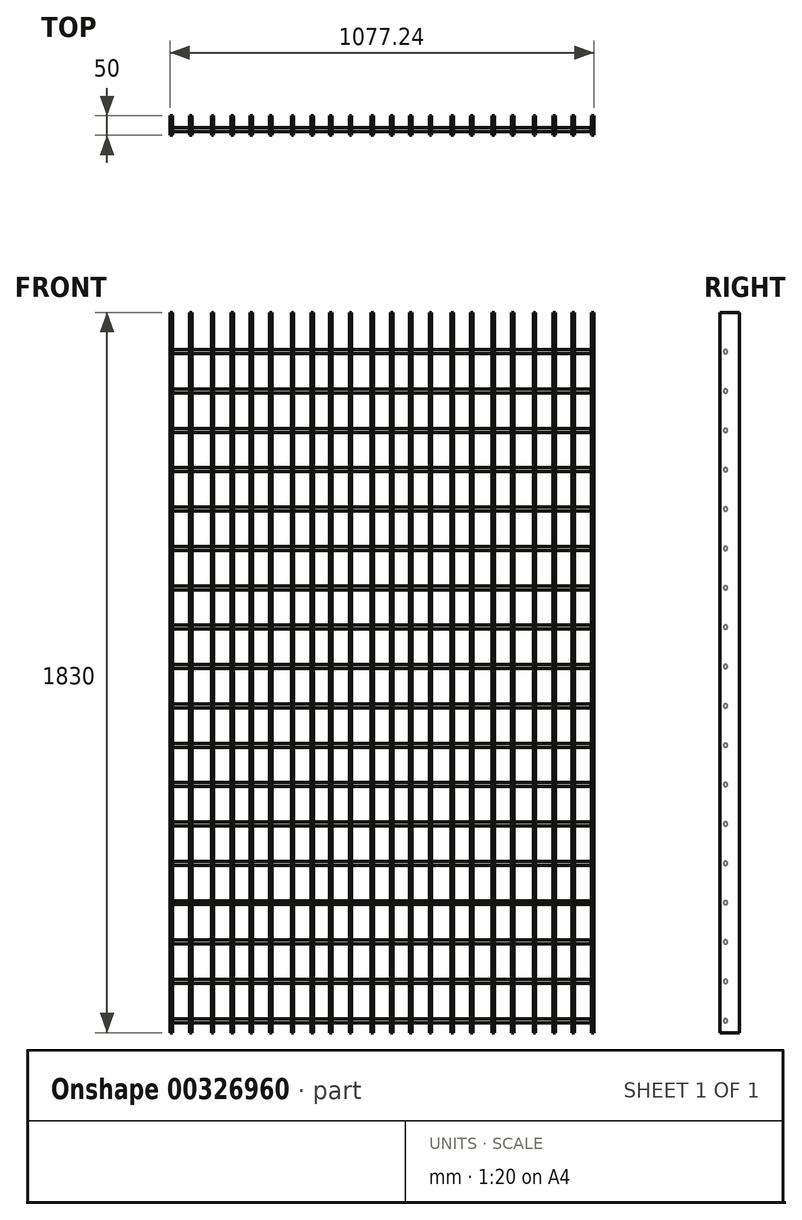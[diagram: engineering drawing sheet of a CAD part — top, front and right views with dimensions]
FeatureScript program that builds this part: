
annotation { "Feature Type Name" : "Feature", "Feature Type Description" : "" }
export const myFeature = defineFeature(function(context is Context, id is Id, definition is map)
    precondition{}
    {
        {
            var Q0;
            Q0=qCreatedBy(makeId("Front.planeOp"),FACE);
            var sketch = newSketch(context, id + "F0", { "sketchPlane" : qUnion([Q0])});
            skLineSegment(sketch, "E0.left", {"start": v(-535, -915) * mm, "end": v(-535, 915) * mm});
            skLineSegment(sketch, "E0.right", {"start": v(535, -915) * mm, "end": v(535, 915) * mm});
            skPoint(sketch, "E0.middle", {"position": v(0, 0) * mm});
            skLineSegment(sketch, "E1", {"start": v(-535, 915) * mm, "end": v(-529, 915) * mm});
            skLineSegment(sketch, "E2", {"start": v(-529, 915) * mm, "end": v(-529, -915) * mm});
            skLineSegment(sketch, "E3", {"start": v(-529, -915) * mm, "end": v(-535, -915) * mm});
            skLineSegment(sketch, "E4", {"start": v(-485, -915) * mm, "end": v(-485, 915) * mm});
            skLineSegment(sketch, "E5", {"start": v(-485, 915) * mm, "end": v(-479, 915) * mm});
            skLineSegment(sketch, "E6", {"start": v(-479, 915) * mm, "end": v(-479, -915) * mm});
            skLineSegment(sketch, "E7", {"start": v(-479, -915) * mm, "end": v(-485, -915) * mm});
            skLineSegment(sketch, "E8.left", {"start": v(-429.8, -915) * mm, "end": v(-429.8, 915) * mm});
            skLineSegment(sketch, "E9", {"start": v(-429.8, 915) * mm, "end": v(-423.8, 915) * mm});
            skLineSegment(sketch, "E10", {"start": v(-423.8, 915) * mm, "end": v(-423.8, -915) * mm});
            skLineSegment(sketch, "E11", {"start": v(-423.8, -915) * mm, "end": v(-429.8, -915) * mm});
            skLineSegment(sketch, "E12", {"start": v(-379.8, -915) * mm, "end": v(-379.8, 915) * mm});
            skLineSegment(sketch, "E13", {"start": v(-379.8, 915) * mm, "end": v(-373.8, 915) * mm});
            skLineSegment(sketch, "E14", {"start": v(-373.8, 915) * mm, "end": v(-373.8, -915) * mm});
            skLineSegment(sketch, "E15", {"start": v(-373.8, -915) * mm, "end": v(-379.8, -915) * mm});
            skLineSegment(sketch, "E16.left", {"start": v(-331.72, -915) * mm, "end": v(-331.72, 915) * mm});
            skLineSegment(sketch, "E17", {"start": v(-331.72, 915) * mm, "end": v(-325.72, 915) * mm});
            skLineSegment(sketch, "E18", {"start": v(-325.72, 915) * mm, "end": v(-325.72, -915) * mm});
            skLineSegment(sketch, "E19", {"start": v(-325.72, -915) * mm, "end": v(-331.72, -915) * mm});
            skLineSegment(sketch, "E20", {"start": v(-281.72, -915) * mm, "end": v(-281.72, 915) * mm});
            skLineSegment(sketch, "E21", {"start": v(-281.72, 915) * mm, "end": v(-275.72, 915) * mm});
            skLineSegment(sketch, "E22", {"start": v(-275.72, 915) * mm, "end": v(-275.72, -915) * mm});
            skLineSegment(sketch, "E23", {"start": v(-275.72, -915) * mm, "end": v(-281.72, -915) * mm});
            skLineSegment(sketch, "E24.left", {"start": v(-226.52, -915) * mm, "end": v(-226.52, 915) * mm});
            skLineSegment(sketch, "E25", {"start": v(-226.52, 915) * mm, "end": v(-220.52, 915) * mm});
            skLineSegment(sketch, "E26", {"start": v(-220.52, 915) * mm, "end": v(-220.52, -915) * mm});
            skLineSegment(sketch, "E27", {"start": v(-220.52, -915) * mm, "end": v(-226.52, -915) * mm});
            skLineSegment(sketch, "E28", {"start": v(-176.52, -915) * mm, "end": v(-176.52, 915) * mm});
            skLineSegment(sketch, "E29", {"start": v(-176.52, 915) * mm, "end": v(-170.52, 915) * mm});
            skLineSegment(sketch, "E30", {"start": v(-170.52, 915) * mm, "end": v(-170.52, -915) * mm});
            skLineSegment(sketch, "E31", {"start": v(-170.52, -915) * mm, "end": v(-176.52, -915) * mm});
            skLineSegment(sketch, "E32.left", {"start": v(-129.52, -915) * mm, "end": v(-129.52, 915) * mm});
            skLineSegment(sketch, "E33", {"start": v(-129.52, 915) * mm, "end": v(-123.52, 915) * mm});
            skLineSegment(sketch, "E34", {"start": v(-123.52, 915) * mm, "end": v(-123.52, -915) * mm});
            skLineSegment(sketch, "E35", {"start": v(-123.52, -915) * mm, "end": v(-129.52, -915) * mm});
            skLineSegment(sketch, "E36", {"start": v(-79.52, -915) * mm, "end": v(-79.52, 915) * mm});
            skLineSegment(sketch, "E37", {"start": v(-79.52, 915) * mm, "end": v(-73.52, 915) * mm});
            skLineSegment(sketch, "E38", {"start": v(-73.52, 915) * mm, "end": v(-73.52, -915) * mm});
            skLineSegment(sketch, "E39", {"start": v(-73.52, -915) * mm, "end": v(-79.52, -915) * mm});
            skLineSegment(sketch, "E40.left", {"start": v(-24.33, -915) * mm, "end": v(-24.33, 915) * mm});
            skLineSegment(sketch, "E41", {"start": v(-24.33, 915) * mm, "end": v(-18.33, 915) * mm});
            skLineSegment(sketch, "E42", {"start": v(-18.33, 915) * mm, "end": v(-18.33, -915) * mm});
            skLineSegment(sketch, "E43", {"start": v(-18.33, -915) * mm, "end": v(-24.33, -915) * mm});
            skLineSegment(sketch, "E44", {"start": v(25.67, -915) * mm, "end": v(25.67, 915) * mm});
            skLineSegment(sketch, "E45", {"start": v(25.67, 915) * mm, "end": v(31.67, 915) * mm});
            skLineSegment(sketch, "E46", {"start": v(31.67, 915) * mm, "end": v(31.67, -915) * mm});
            skLineSegment(sketch, "E47", {"start": v(31.67, -915) * mm, "end": v(25.67, -915) * mm});
            skLineSegment(sketch, "E48.left", {"start": v(73.76, -915) * mm, "end": v(73.76, 915) * mm});
            skLineSegment(sketch, "E49", {"start": v(73.76, 915) * mm, "end": v(79.76, 915) * mm});
            skLineSegment(sketch, "E50", {"start": v(79.76, 915) * mm, "end": v(79.76, -915) * mm});
            skLineSegment(sketch, "E51", {"start": v(79.76, -915) * mm, "end": v(73.76, -915) * mm});
            skLineSegment(sketch, "E52", {"start": v(123.76, -915) * mm, "end": v(123.76, 915) * mm});
            skLineSegment(sketch, "E53", {"start": v(123.76, 915) * mm, "end": v(129.76, 915) * mm});
            skLineSegment(sketch, "E54", {"start": v(129.76, 915) * mm, "end": v(129.76, -915) * mm});
            skLineSegment(sketch, "E55", {"start": v(129.76, -915) * mm, "end": v(123.76, -915) * mm});
            skLineSegment(sketch, "E56.left", {"start": v(178.95, -915) * mm, "end": v(178.95, 915) * mm});
            skLineSegment(sketch, "E57", {"start": v(178.95, 915) * mm, "end": v(184.95, 915) * mm});
            skLineSegment(sketch, "E58", {"start": v(184.95, 915) * mm, "end": v(184.95, -915) * mm});
            skLineSegment(sketch, "E59", {"start": v(184.95, -915) * mm, "end": v(178.95, -915) * mm});
            skLineSegment(sketch, "E60", {"start": v(228.95, -915) * mm, "end": v(228.95, 915) * mm});
            skLineSegment(sketch, "E61", {"start": v(228.95, 915) * mm, "end": v(234.95, 915) * mm});
            skLineSegment(sketch, "E62", {"start": v(234.95, 915) * mm, "end": v(234.95, -915) * mm});
            skLineSegment(sketch, "E63", {"start": v(234.95, -915) * mm, "end": v(228.95, -915) * mm});
            skLineSegment(sketch, "E64.left", {"start": v(282.95, -915) * mm, "end": v(282.95, 915) * mm});
            skLineSegment(sketch, "E65", {"start": v(282.95, 915) * mm, "end": v(288.95, 915) * mm});
            skLineSegment(sketch, "E66", {"start": v(288.95, 915) * mm, "end": v(288.95, -915) * mm});
            skLineSegment(sketch, "E67", {"start": v(288.95, -915) * mm, "end": v(282.95, -915) * mm});
            skLineSegment(sketch, "E68", {"start": v(332.95, -915) * mm, "end": v(332.95, 915) * mm});
            skLineSegment(sketch, "E69", {"start": v(332.95, 915) * mm, "end": v(338.95, 915) * mm});
            skLineSegment(sketch, "E70", {"start": v(338.95, 915) * mm, "end": v(338.95, -915) * mm});
            skLineSegment(sketch, "E71", {"start": v(338.95, -915) * mm, "end": v(332.95, -915) * mm});
            skLineSegment(sketch, "E72.left", {"start": v(388.15, -915) * mm, "end": v(388.15, 915) * mm});
            skLineSegment(sketch, "E73", {"start": v(388.15, 915) * mm, "end": v(394.15, 915) * mm});
            skLineSegment(sketch, "E74", {"start": v(394.15, 915) * mm, "end": v(394.15, -915) * mm});
            skLineSegment(sketch, "E75", {"start": v(394.15, -915) * mm, "end": v(388.15, -915) * mm});
            skLineSegment(sketch, "E76", {"start": v(438.15, -915) * mm, "end": v(438.15, 915) * mm});
            skLineSegment(sketch, "E77", {"start": v(438.15, 915) * mm, "end": v(444.15, 915) * mm});
            skLineSegment(sketch, "E78", {"start": v(444.15, 915) * mm, "end": v(444.15, -915) * mm});
            skLineSegment(sketch, "E79", {"start": v(444.15, -915) * mm, "end": v(438.15, -915) * mm});
            skLineSegment(sketch, "E80.left", {"start": v(486.24, -915) * mm, "end": v(486.24, 915) * mm});
            skLineSegment(sketch, "E81", {"start": v(486.24, 915) * mm, "end": v(492.24, 915) * mm});
            skLineSegment(sketch, "E82", {"start": v(492.24, 915) * mm, "end": v(492.24, -915) * mm});
            skLineSegment(sketch, "E83", {"start": v(492.24, -915) * mm, "end": v(486.24, -915) * mm});
            skLineSegment(sketch, "E84", {"start": v(536.24, -915) * mm, "end": v(536.24, 915) * mm});
            skLineSegment(sketch, "E85", {"start": v(536.24, 915) * mm, "end": v(542.24, 915) * mm});
            skLineSegment(sketch, "E86", {"start": v(542.24, 915) * mm, "end": v(542.24, -915) * mm});
            skLineSegment(sketch, "E87", {"start": v(542.24, -915) * mm, "end": v(536.24, -915) * mm});
            skSolve(sketch);
        }
        {
            var Q0;
            Q0 = qSketchRegion(id + "F0", true);
            extrude(context, id + "F1", {"entities" : qUnion([Q0]), "depth" : 50 * mm});
        }
        {
            var Q0;
            Q0=qCreatedBy(makeId("Right.planeOp"),FACE);
            var sketch = newSketch(context, id + "F2", { "sketchPlane" : qUnion([Q0])});
            skLineSegment(sketch, "E88", {"start": v(-49.74, 915.3) * mm, "end": v(-35.74, 915.3) * mm});
            skLineSegment(sketch, "E89", {"start": v(-35.74, 915.3) * mm, "end": v(-35.74, 815.3) * mm});
            skLineSegment(sketch, "E90", {"start": v(-35.74, 815.3) * mm, "end": v(-35.74, 715.3) * mm});
            skLineSegment(sketch, "E91", {"start": v(-35.74, 715.3) * mm, "end": v(-35.74, 615.3) * mm});
            skLineSegment(sketch, "E92", {"start": v(-35.74, 615.3) * mm, "end": v(-35.74, 515.3) * mm});
            skLineSegment(sketch, "E93", {"start": v(-35.74, 515.3) * mm, "end": v(-35.74, 415.3) * mm});
            skLineSegment(sketch, "E94", {"start": v(-35.74, 415.3) * mm, "end": v(-35.74, 315.3) * mm});
            skLineSegment(sketch, "E95", {"start": v(-35.74, 315.3) * mm, "end": v(-35.74, 215.3) * mm});
            skLineSegment(sketch, "E96", {"start": v(-35.74, 215.3) * mm, "end": v(-35.74, 115.3) * mm});
            skLineSegment(sketch, "E97", {"start": v(-35.74, 115.3) * mm, "end": v(-35.74, 15.3) * mm});
            skLineSegment(sketch, "E98", {"start": v(-35.74, 15.3) * mm, "end": v(-35.74, -84.7) * mm});
            skLineSegment(sketch, "E99", {"start": v(-35.74, -84.7) * mm, "end": v(-35.74, -184.7) * mm});
            skLineSegment(sketch, "E100", {"start": v(-35.74, -184.7) * mm, "end": v(-35.74, -284.7) * mm});
            skLineSegment(sketch, "E101", {"start": v(-35.74, -284.7) * mm, "end": v(-35.74, -384.7) * mm});
            skLineSegment(sketch, "E102", {"start": v(-35.74, -384.7) * mm, "end": v(-35.74, -484.7) * mm});
            skLineSegment(sketch, "E103", {"start": v(-35.74, -484.7) * mm, "end": v(-35.74, -584.7) * mm});
            skLineSegment(sketch, "E104", {"start": v(-35.74, -584.7) * mm, "end": v(-35.74, -684.7) * mm});
            skLineSegment(sketch, "E105", {"start": v(-35.74, -684.7) * mm, "end": v(-35.74, -784.7) * mm});
            skLineSegment(sketch, "E106", {"start": v(-35.74, -784.7) * mm, "end": v(-35.74, -884.7) * mm});
            skCircle(sketch, "E107", {"center": v(-35.74, 815.3) * mm, "radius": 5 * mm});
            skCircle(sketch, "E108", {"center": v(-35.74, 715.3) * mm, "radius": 5 * mm});
            skCircle(sketch, "E109", {"center": v(-35.74, 615.3) * mm, "radius": 5 * mm});
            skCircle(sketch, "E110", {"center": v(-35.74, 515.3) * mm, "radius": 5 * mm});
            skCircle(sketch, "E111", {"center": v(-35.74, 415.3) * mm, "radius": 5 * mm});
            skCircle(sketch, "E112", {"center": v(-35.74, 315.3) * mm, "radius": 5 * mm});
            skCircle(sketch, "E113", {"center": v(-35.74, 215.3) * mm, "radius": 5 * mm});
            skCircle(sketch, "E114", {"center": v(-35.74, 115.3) * mm, "radius": 5 * mm});
            skCircle(sketch, "E115", {"center": v(-35.74, 15.3) * mm, "radius": 5 * mm});
            skCircle(sketch, "E116", {"center": v(-35.74, -84.7) * mm, "radius": 5 * mm});
            skCircle(sketch, "E117", {"center": v(-35.74, -184.7) * mm, "radius": 5 * mm});
            skCircle(sketch, "E118", {"center": v(-35.74, -284.7) * mm, "radius": 5 * mm});
            skCircle(sketch, "E119", {"center": v(-35.74, -384.7) * mm, "radius": 5 * mm});
            skCircle(sketch, "E120", {"center": v(-35.74, -484.7) * mm, "radius": 5 * mm});
            skCircle(sketch, "E121", {"center": v(-35.74, -584.7) * mm, "radius": 5 * mm});
            skCircle(sketch, "E122", {"center": v(-35.74, -684.7) * mm, "radius": 5 * mm});
            skCircle(sketch, "E123", {"center": v(-35.74, -784.7) * mm, "radius": 5 * mm});
            skCircle(sketch, "E124", {"center": v(-35.74, -884.7) * mm, "radius": 5 * mm});
            skSolve(sketch);
        }
        {
            var Q0;
            Q0 = qSketchRegion(id + "F2", true);
            extrude(context, id + "F3", {"entities" : qUnion([Q0]), "endBound" : BoundingType.SYMMETRIC, "depth" : 1070 * mm});
        }
    });
